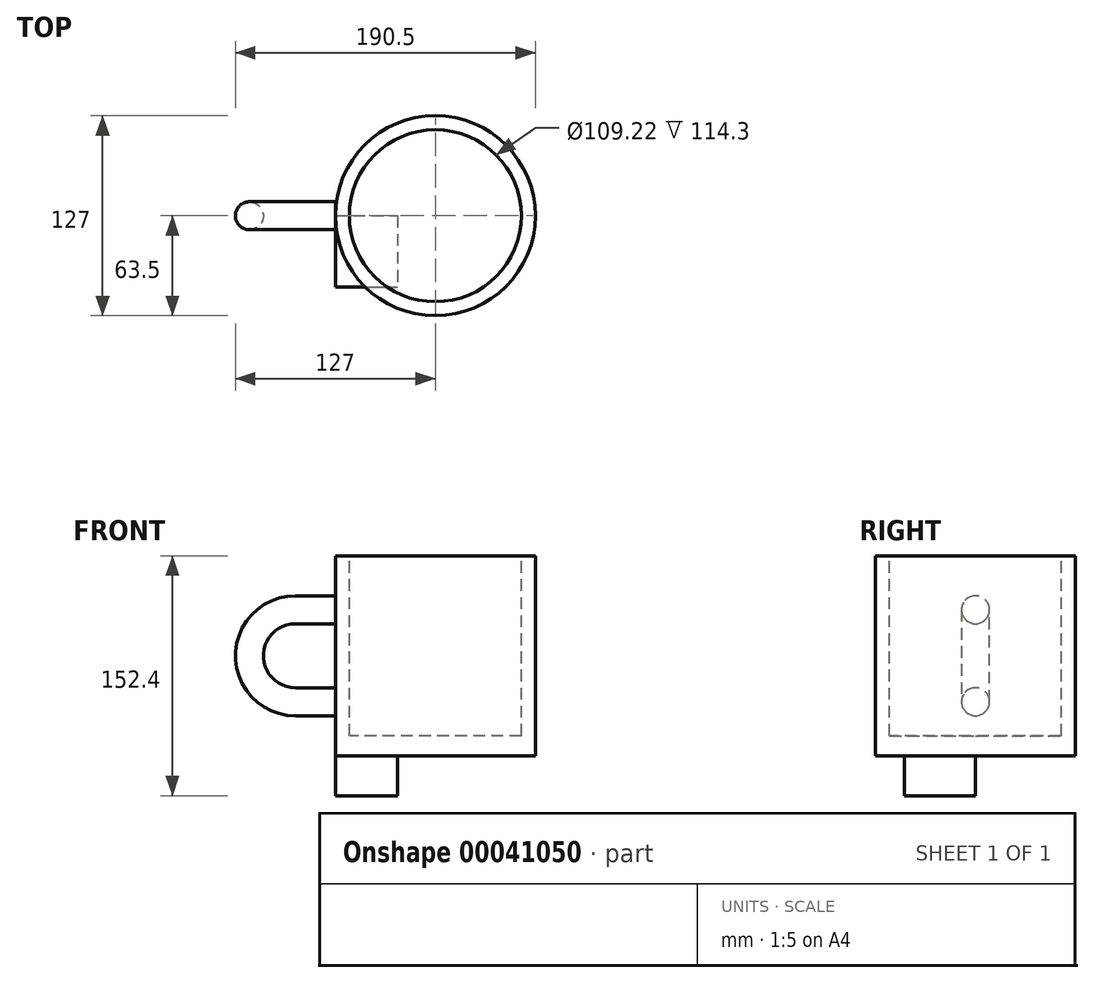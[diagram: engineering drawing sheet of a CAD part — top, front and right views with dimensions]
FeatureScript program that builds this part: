
annotation { "Feature Type Name" : "Feature", "Feature Type Description" : "" }
export const myFeature = defineFeature(function(context is Context, id is Id, definition is map)
    precondition{}
    {
        {
            var Q0;
            Q0=qCreatedBy(makeId("Top.planeOp"),FACE);
            var sketch = newSketch(context, id + "F0", { "sketchPlane" : qUnion([Q0])});
            skCircle(sketch, "E0", {"center": v(0, 0) * mm, "radius": 63.5 * mm});
            skSolve(sketch);
        }
        {
            var Q0;
            Q0=makeQuery(id+"F0.imprint","IMPRINT",FACE,{"disambiguationData":[TD([[makeQuery(id+"F0.imprint","IMPRINT",EDGE,{"derivedFrom":sQuery(id+"F0.wireOp",EDGE,"E0")}),1.0]])]});
            extrude(context, id + "F1", {"entities" : qUnion([Q0]), "depth" : 127 * mm});
        }
        {
            var Q0;
            Q0=makeQuery(id+"F1.opExtrude","CAP_FACE",FACE,{"disambiguationData":[OSD([sQuery(id+"F0.wireOp",EDGE,"E0")])],"isStart":false});
            var sketch = newSketch(context, id + "F2", { "sketchPlane" : qUnion([Q0])});
            skCircle(sketch, "E1", {"center": v(0, 0) * mm, "radius": 54.61 * mm});
            skSolve(sketch);
        }
        {
            var Q0;
            Q0 = qSketchRegion(id + "F2", true);
            extrude(context, id + "F3", {"entities" : qUnion([Q0]), "operationType" : NewBodyOperationType.REMOVE, "oppositeDirection" : true, "depth" : 114.3 * mm});
        }
        {
            var Q0;
            Q0=makeQuery(id+"F1.opExtrude","CAP_FACE",FACE,{"disambiguationData":[OSD([sQuery(id+"F0.wireOp",EDGE,"E0")])],"isStart":true});
            var sketch = newSketch(context, id + "F4", { "sketchPlane" : qUnion([Q0])});
            skLineSegment(sketch, "E2.bottom", {"start": v(-63.5, 0) * mm, "end": v(-23.9, 0) * mm});
            skLineSegment(sketch, "E2.top", {"start": v(-63.5, 45.22) * mm, "end": v(-23.9, 45.22) * mm});
            skLineSegment(sketch, "E2.left", {"start": v(-63.5, 0) * mm, "end": v(-63.5, 45.22) * mm});
            skLineSegment(sketch, "E2.right", {"start": v(-23.9, 0) * mm, "end": v(-23.9, 45.22) * mm});
            skSolve(sketch);
        }
        {
            var Q0;
            Q0 = qSketchRegion(id + "F4", true);
            extrude(context, id + "F5", {"entities" : qUnion([Q0]), "operationType" : NewBodyOperationType.ADD, "depth" : 25.4 * mm});
        }
        {
            var Q0;
            Q0=makeQuery(id+"F5.opExtrude","SWEPT_FACE",FACE,{"disambiguationData":[OSD([sQuery(id+"F4.wireOp",EDGE,"E2.left")])]});
            var sketch = newSketch(context, id + "F6", { "sketchPlane" : qUnion([Q0])});
            skCircle(sketch, "E3", {"center": v(0, 34.3) * mm, "radius": 8.9 * mm});
            skCircle(sketch, "E4", {"center": v(0, 92.7) * mm, "radius": 8.9 * mm});
            skSolve(sketch);
        }
        {
            var Q0;
            Q0=makeQuery(id+"F6.imprint","IMPRINT",FACE,{"disambiguationData":[TD([[makeQuery(id+"F6.imprint","IMPRINT",EDGE,{"derivedFrom":sQuery(id+"F6.wireOp",EDGE,"E4")}),1.0]])]});
            var Q1;
            Q1=makeQuery(id+"F6.imprint","IMPRINT",FACE,{"disambiguationData":[TD([[makeQuery(id+"F6.imprint","IMPRINT",EDGE,{"derivedFrom":sQuery(id+"F6.wireOp",EDGE,"E3")}),1.0]])]});
            extrude(context, id + "F7", {"entities" : qUnion([Q0, Q1]), "operationType" : NewBodyOperationType.ADD, "depth" : 25.4 * mm});
        }
        {
            var Q0;
            Q0=makeQuery(id+"F7.opExtrude","CAP_FACE",FACE,{"disambiguationData":[OSD([sQuery(id+"F6.wireOp",EDGE,"E4")])],"isStart":false});
            var sketch = newSketch(context, id + "F8", { "sketchPlane" : qUnion([Q0])});
            skLineSegment(sketch, "E5", {"start": v(-40.4, 63.5) * mm, "end": v(39.58, 63.5) * mm});
            skSolve(sketch);
        }
        {
            var Q0;
            Q0=makeQuery(id+"F8.imprint","IMPRINT",FACE,{"disambiguationData":[TD([[makeQuery(id+"F8.imprint","IMPRINT",EDGE,{"derivedFrom":makeQuery(id+"F7.opExtrude","CAP_EDGE",EDGE,{"disambiguationData":[OSD([sQuery(id+"F6.wireOp",EDGE,"E4")])],"isStart":false})}),1.0]])]});
            var Q1;
            Q1=sQuery(id+"F8.wireOp",EDGE,"E5");
            revolve(context, id + "F9", {"operationType" : NewBodyOperationType.ADD, "entities" : qUnion([Q0]), "axis" : qUnion([Q1]), "revolveType" : RevolveType.ONE_DIRECTION, "angle" : 180 * degree});
        }
    });
